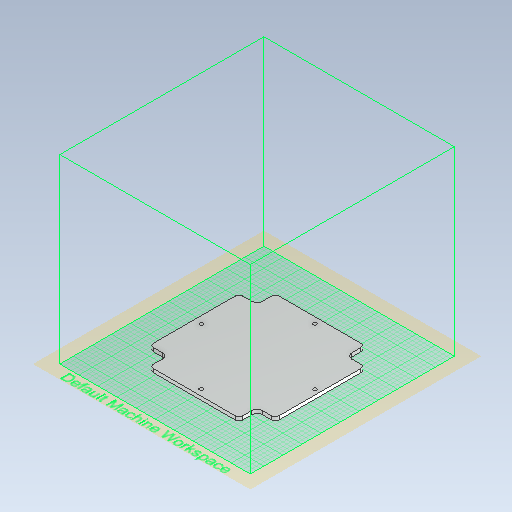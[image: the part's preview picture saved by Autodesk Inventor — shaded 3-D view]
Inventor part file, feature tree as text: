
AUTODESK INVENTOR PART (.ipt)
format: ipt  version: 2021 (Build 250183000, 183)  size: 347,648 bytes
history: native  units: mm
features: other x2, plane x1, extrude x1, sketch x1, reference x1, projected_geometry x1
ambient origin geometry x8: Origin, YZ Plane, XZ Plane, XY Plane, X Axis, Y Axis, Z Axis, Center Point
bodies: Body1 (feature_tree)
feature tree (7):
  plane  "Work Plane1"
  extrude  "Extrusion3"  Depth=277.0mm
  sketch  "Sketch6"  dims[d19=8.0mm d20=0.0mm d21=1.5mm d31=4.5mm d32=4.5mm d33=4.5mm d34=15.0mm d35=15.0mm d36=15.0mm d37=25.0mm d38=25.0mm d39=25.0mm d40=138.5mm d41=277.0mm]
  reference  "Reference1"
  projected_geometry  "Projected Loop3"
  other  "Assembly1"
  other  "MDF_Block:1"
